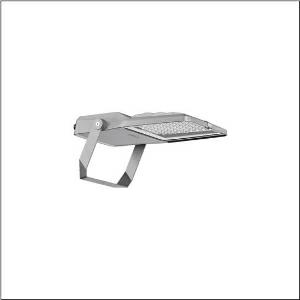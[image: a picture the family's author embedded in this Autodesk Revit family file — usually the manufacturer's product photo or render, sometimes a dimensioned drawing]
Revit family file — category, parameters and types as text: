
# Revit family: floodlight_fl_21_mini___pl43_5xa7772b5a1a_a18d
name_source: partatom
category: Lighting Fixtures
units: mm (PartAtom-declared; Revit-internal decimal feet)

## family parameters
Cut with Voids When Loaded = No
Host = Face
Light Source = No
Part Type = Normal
Room Calculation Point = No
Round Connector Dimension = Use Diameter
Shared = No

## types (1)
- --- (1 x LED, 5970 lm, 45.5 W, 4000K)
    Apparent Load = 46 VA
    CIE Flux Codes = 27 78 99 100 100
    Color Rendering = 80
    Color Temperature = 4000K
    Default Elevation = 1800 mm
    Description = Floodlight FL 21 mini, floodlight, primary light control with lens, of PMMA, primary optical cover: protective disc, of toughened safety glass, transparent, light distribution: PL43, light emission: direct distribution, installation type: surface-mounted, LED, High Power LED, rated luminous flux: 5.970lm, luminous efficacy: 131lm/W, light colour: 840, colour temperature: 4000K, control gear: ECG iQ, control: Street-Remote, Auto-Match, Temp-Guard, Night-Set, Smart-Wire, Desk-Remote (wireless, voltage-free reading and setting of iQ features in the workshop via application-optimized NFC function/RFID function), optimised constant luminous flux control (CLO 2.0), with terminal, 6-pole, mains connection: 220..240V, AC, 50/60Hz, start of lifetime: 46W, end of lifetime: 48W, reduction: 22W, luminaire housing, of diecast aluminium, powder-coated, Siteco® metallic grey (DB 702S), corrosivity category C5 according to DIN EN ISO 12944, mounting bracket, of steel, galvanised, powder-coated, Siteco® metallic grey (DB 702S), protection rating (complete): IP66, insulation class (complete): insulation class II (safety insulation), certification: CE, ENEC, VDE, protection symbol: D, impact resistance: IK08, permissible operating ambient temperature: -40..+40°C, permissible operating ambient temperature for outdoor applications: -40..+50°C, standard: DIN EN 12944, packaging unit: 1 piece

Light Distribution: PL43
    Height = 70 mm
    Lamp = 1 x LED
    Lamp Light Flux = 5970 lm
    Lamp Power = 45.5 W
    Lamp count = 1
    Length = 485 mm
    Luminous efficacy = 131 lm/W
    Manufacturer = Siteco
    ModVariant = No
    Model = 5XA7772B5A1A
    Number of Poles = 1
    OnlyDefault = Yes
    Power Factor = 1
    Product Name = Floodlight FL 21 mini | PL43
    Product group = floodlight | pylon top
    ProductGroupID = 6101
    Protection Class = Protection class II
    Protection Degree = IP 66
    RLX_Detail_Level = 1
    RlxData = <blob elided: 95969 chars, md5=7bb1f72f>
    Socket = socket
    Standby Power = 0 W
    System Light Flux = 5970 lm
    System Power = 46 W
    Type Comments = factory setting: luminous flux: 100 % | dim-lin: 254 | 463 mA
    Type Image = l_1006845.jpg
    URL = http://relux.com
    VarID = @adj_073833
    Voltage = 0 V
    Weight = 0.00 kg
    Width = 337 mm

## geometry (parser evidence)
native form markers: Blend x4, Sweep x14
no freeform markers — native parametric forms only
